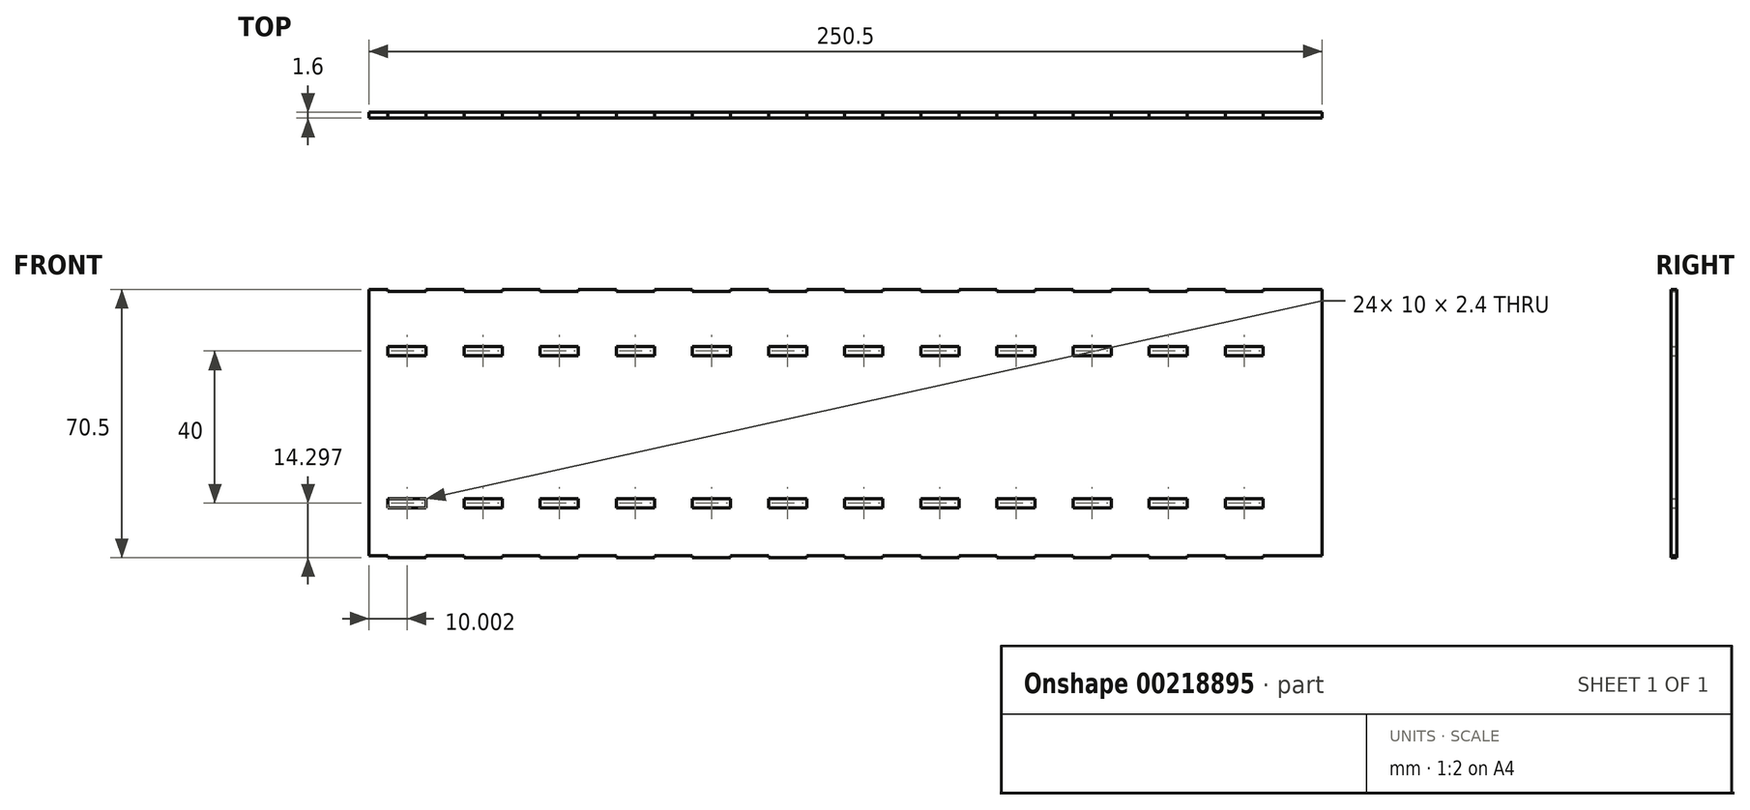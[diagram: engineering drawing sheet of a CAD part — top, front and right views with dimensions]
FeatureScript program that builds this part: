
annotation { "Feature Type Name" : "Feature", "Feature Type Description" : "" }
export const myFeature = defineFeature(function(context is Context, id is Id, definition is map)
    precondition{}
    {
        {
            var Q0;
            Q0=qCreatedBy(makeId("Front.planeOp"),FACE);
            var sketch = newSketch(context, id + "F0", { "sketchPlane" : qUnion([Q0])});
            skLineSegment(sketch, "E0.top", {"start": v(-125.84, -55.1) * mm, "end": v(-120.84, -55.1) * mm});
            skLineSegment(sketch, "E0.left", {"start": v(-125.84, 14.9) * mm, "end": v(-125.84, -55.1) * mm});
            skLineSegment(sketch, "E0.right", {"start": v(124.66, 14.9) * mm, "end": v(124.66, -55.1) * mm});
            skLineSegment(sketch, "E1.bottom", {"start": v(-120.84, -0.1) * mm, "end": v(-110.84, -0.1) * mm});
            skLineSegment(sketch, "E1.top", {"start": v(-120.84, -2.5) * mm, "end": v(-110.84, -2.5) * mm});
            skLineSegment(sketch, "E1.left", {"start": v(-120.84, -0.1) * mm, "end": v(-120.84, -2.5) * mm});
            skLineSegment(sketch, "E1.right", {"start": v(-110.84, -0.1) * mm, "end": v(-110.84, -2.5) * mm});
            skLineSegment(sketch, "E2.bottom", {"start": v(-120.84, -40.1) * mm, "end": v(-110.84, -40.1) * mm});
            skLineSegment(sketch, "E2.top", {"start": v(-120.84, -42.5) * mm, "end": v(-110.84, -42.5) * mm});
            skLineSegment(sketch, "E2.left", {"start": v(-120.84, -40.1) * mm, "end": v(-120.84, -42.5) * mm});
            skLineSegment(sketch, "E2.right", {"start": v(-110.84, -40.1) * mm, "end": v(-110.84, -42.5) * mm});
            skLineSegment(sketch, "E3.1.0.0", {"start": v(-100.84, -0.1) * mm, "end": v(-90.84, -0.1) * mm});
            skLineSegment(sketch, "E3.1.0.1", {"start": v(-100.84, -2.5) * mm, "end": v(-90.84, -2.5) * mm});
            skLineSegment(sketch, "E3.1.0.2", {"start": v(-90.84, -0.1) * mm, "end": v(-90.84, -2.5) * mm});
            skLineSegment(sketch, "E3.1.0.3", {"start": v(-100.84, -0.1) * mm, "end": v(-100.84, -2.5) * mm});
            skLineSegment(sketch, "E3.1.0.4", {"start": v(-100.84, -42.5) * mm, "end": v(-90.84, -42.5) * mm});
            skLineSegment(sketch, "E3.1.0.5", {"start": v(-100.84, -40.1) * mm, "end": v(-90.84, -40.1) * mm});
            skLineSegment(sketch, "E3.1.0.6", {"start": v(-90.84, -40.1) * mm, "end": v(-90.84, -42.5) * mm});
            skLineSegment(sketch, "E3.1.0.7", {"start": v(-100.84, -40.1) * mm, "end": v(-100.84, -42.5) * mm});
            skLineSegment(sketch, "E3.2.0.0", {"start": v(-80.84, -0.1) * mm, "end": v(-70.84, -0.1) * mm});
            skLineSegment(sketch, "E3.2.0.1", {"start": v(-80.84, -2.5) * mm, "end": v(-70.84, -2.5) * mm});
            skLineSegment(sketch, "E3.2.0.2", {"start": v(-70.84, -0.1) * mm, "end": v(-70.84, -2.5) * mm});
            skLineSegment(sketch, "E3.2.0.3", {"start": v(-80.84, -0.1) * mm, "end": v(-80.84, -2.5) * mm});
            skLineSegment(sketch, "E3.2.0.4", {"start": v(-80.84, -42.5) * mm, "end": v(-70.84, -42.5) * mm});
            skLineSegment(sketch, "E3.2.0.5", {"start": v(-80.84, -40.1) * mm, "end": v(-70.84, -40.1) * mm});
            skLineSegment(sketch, "E3.2.0.6", {"start": v(-70.84, -40.1) * mm, "end": v(-70.84, -42.5) * mm});
            skLineSegment(sketch, "E3.2.0.7", {"start": v(-80.84, -40.1) * mm, "end": v(-80.84, -42.5) * mm});
            skLineSegment(sketch, "E3.3.0.0", {"start": v(-60.84, -0.1) * mm, "end": v(-50.84, -0.1) * mm});
            skLineSegment(sketch, "E3.3.0.1", {"start": v(-60.84, -2.5) * mm, "end": v(-50.84, -2.5) * mm});
            skLineSegment(sketch, "E3.3.0.2", {"start": v(-50.84, -0.1) * mm, "end": v(-50.84, -2.5) * mm});
            skLineSegment(sketch, "E3.3.0.3", {"start": v(-60.84, -0.1) * mm, "end": v(-60.84, -2.5) * mm});
            skLineSegment(sketch, "E3.3.0.4", {"start": v(-60.84, -42.5) * mm, "end": v(-50.84, -42.5) * mm});
            skLineSegment(sketch, "E3.3.0.5", {"start": v(-60.84, -40.1) * mm, "end": v(-50.84, -40.1) * mm});
            skLineSegment(sketch, "E3.3.0.6", {"start": v(-50.84, -40.1) * mm, "end": v(-50.84, -42.5) * mm});
            skLineSegment(sketch, "E3.3.0.7", {"start": v(-60.84, -40.1) * mm, "end": v(-60.84, -42.5) * mm});
            skLineSegment(sketch, "E3.4.0.0", {"start": v(-40.84, -0.1) * mm, "end": v(-30.84, -0.1) * mm});
            skLineSegment(sketch, "E3.4.0.1", {"start": v(-40.84, -2.5) * mm, "end": v(-30.84, -2.5) * mm});
            skLineSegment(sketch, "E3.4.0.2", {"start": v(-30.84, -0.1) * mm, "end": v(-30.84, -2.5) * mm});
            skLineSegment(sketch, "E3.4.0.3", {"start": v(-40.84, -0.1) * mm, "end": v(-40.84, -2.5) * mm});
            skLineSegment(sketch, "E3.4.0.4", {"start": v(-40.84, -42.5) * mm, "end": v(-30.84, -42.5) * mm});
            skLineSegment(sketch, "E3.4.0.5", {"start": v(-40.84, -40.1) * mm, "end": v(-30.84, -40.1) * mm});
            skLineSegment(sketch, "E3.4.0.6", {"start": v(-30.84, -40.1) * mm, "end": v(-30.84, -42.5) * mm});
            skLineSegment(sketch, "E3.4.0.7", {"start": v(-40.84, -40.1) * mm, "end": v(-40.84, -42.5) * mm});
            skLineSegment(sketch, "E3.5.0.0", {"start": v(-20.84, -0.1) * mm, "end": v(-10.84, -0.1) * mm});
            skLineSegment(sketch, "E3.5.0.1", {"start": v(-20.84, -2.5) * mm, "end": v(-10.84, -2.5) * mm});
            skLineSegment(sketch, "E3.5.0.2", {"start": v(-10.84, -0.1) * mm, "end": v(-10.84, -2.5) * mm});
            skLineSegment(sketch, "E3.5.0.3", {"start": v(-20.84, -0.1) * mm, "end": v(-20.84, -2.5) * mm});
            skLineSegment(sketch, "E3.5.0.4", {"start": v(-20.84, -42.5) * mm, "end": v(-10.84, -42.5) * mm});
            skLineSegment(sketch, "E3.5.0.5", {"start": v(-20.84, -40.1) * mm, "end": v(-10.84, -40.1) * mm});
            skLineSegment(sketch, "E3.5.0.6", {"start": v(-10.84, -40.1) * mm, "end": v(-10.84, -42.5) * mm});
            skLineSegment(sketch, "E3.5.0.7", {"start": v(-20.84, -40.1) * mm, "end": v(-20.84, -42.5) * mm});
            skLineSegment(sketch, "E3.6.0.0", {"start": v(-0.84, -0.1) * mm, "end": v(9.16, -0.1) * mm});
            skLineSegment(sketch, "E3.6.0.1", {"start": v(-0.84, -2.5) * mm, "end": v(9.16, -2.5) * mm});
            skLineSegment(sketch, "E3.6.0.2", {"start": v(9.16, -0.1) * mm, "end": v(9.16, -2.5) * mm});
            skLineSegment(sketch, "E3.6.0.3", {"start": v(-0.84, -0.1) * mm, "end": v(-0.84, -2.5) * mm});
            skLineSegment(sketch, "E3.6.0.4", {"start": v(-0.84, -42.5) * mm, "end": v(9.16, -42.5) * mm});
            skLineSegment(sketch, "E3.6.0.5", {"start": v(-0.84, -40.1) * mm, "end": v(9.16, -40.1) * mm});
            skLineSegment(sketch, "E3.6.0.6", {"start": v(9.16, -40.1) * mm, "end": v(9.16, -42.5) * mm});
            skLineSegment(sketch, "E3.6.0.7", {"start": v(-0.84, -40.1) * mm, "end": v(-0.84, -42.5) * mm});
            skLineSegment(sketch, "E3.7.0.0", {"start": v(19.16, -0.1) * mm, "end": v(29.16, -0.1) * mm});
            skLineSegment(sketch, "E3.7.0.1", {"start": v(19.16, -2.5) * mm, "end": v(29.16, -2.5) * mm});
            skLineSegment(sketch, "E3.7.0.2", {"start": v(29.16, -0.1) * mm, "end": v(29.16, -2.5) * mm});
            skLineSegment(sketch, "E3.7.0.3", {"start": v(19.16, -0.1) * mm, "end": v(19.16, -2.5) * mm});
            skLineSegment(sketch, "E3.7.0.4", {"start": v(19.16, -42.5) * mm, "end": v(29.16, -42.5) * mm});
            skLineSegment(sketch, "E3.7.0.5", {"start": v(19.16, -40.1) * mm, "end": v(29.16, -40.1) * mm});
            skLineSegment(sketch, "E3.7.0.6", {"start": v(29.16, -40.1) * mm, "end": v(29.16, -42.5) * mm});
            skLineSegment(sketch, "E3.7.0.7", {"start": v(19.16, -40.1) * mm, "end": v(19.16, -42.5) * mm});
            skLineSegment(sketch, "E3.8.0.0", {"start": v(39.16, -0.1) * mm, "end": v(49.16, -0.1) * mm});
            skLineSegment(sketch, "E3.8.0.1", {"start": v(39.16, -2.5) * mm, "end": v(49.16, -2.5) * mm});
            skLineSegment(sketch, "E3.8.0.2", {"start": v(49.16, -0.1) * mm, "end": v(49.16, -2.5) * mm});
            skLineSegment(sketch, "E3.8.0.3", {"start": v(39.16, -0.1) * mm, "end": v(39.16, -2.5) * mm});
            skLineSegment(sketch, "E3.8.0.4", {"start": v(39.16, -42.5) * mm, "end": v(49.16, -42.5) * mm});
            skLineSegment(sketch, "E3.8.0.5", {"start": v(39.16, -40.1) * mm, "end": v(49.16, -40.1) * mm});
            skLineSegment(sketch, "E3.8.0.6", {"start": v(49.16, -40.1) * mm, "end": v(49.16, -42.5) * mm});
            skLineSegment(sketch, "E3.8.0.7", {"start": v(39.16, -40.1) * mm, "end": v(39.16, -42.5) * mm});
            skLineSegment(sketch, "E3.9.0.0", {"start": v(59.16, -0.1) * mm, "end": v(69.16, -0.1) * mm});
            skLineSegment(sketch, "E3.9.0.1", {"start": v(59.16, -2.5) * mm, "end": v(69.16, -2.5) * mm});
            skLineSegment(sketch, "E3.9.0.2", {"start": v(69.16, -0.1) * mm, "end": v(69.16, -2.5) * mm});
            skLineSegment(sketch, "E3.9.0.3", {"start": v(59.16, -0.1) * mm, "end": v(59.16, -2.5) * mm});
            skLineSegment(sketch, "E3.9.0.4", {"start": v(59.16, -42.5) * mm, "end": v(69.16, -42.5) * mm});
            skLineSegment(sketch, "E3.9.0.5", {"start": v(59.16, -40.1) * mm, "end": v(69.16, -40.1) * mm});
            skLineSegment(sketch, "E3.9.0.6", {"start": v(69.16, -40.1) * mm, "end": v(69.16, -42.5) * mm});
            skLineSegment(sketch, "E3.9.0.7", {"start": v(59.16, -40.1) * mm, "end": v(59.16, -42.5) * mm});
            skLineSegment(sketch, "E3.10.0.0", {"start": v(79.16, -0.1) * mm, "end": v(89.16, -0.1) * mm});
            skLineSegment(sketch, "E3.10.0.1", {"start": v(79.16, -2.5) * mm, "end": v(89.16, -2.5) * mm});
            skLineSegment(sketch, "E3.10.0.2", {"start": v(89.16, -0.1) * mm, "end": v(89.16, -2.5) * mm});
            skLineSegment(sketch, "E3.10.0.3", {"start": v(79.16, -0.1) * mm, "end": v(79.16, -2.5) * mm});
            skLineSegment(sketch, "E3.10.0.4", {"start": v(79.16, -42.5) * mm, "end": v(89.16, -42.5) * mm});
            skLineSegment(sketch, "E3.10.0.5", {"start": v(79.16, -40.1) * mm, "end": v(89.16, -40.1) * mm});
            skLineSegment(sketch, "E3.10.0.6", {"start": v(89.16, -40.1) * mm, "end": v(89.16, -42.5) * mm});
            skLineSegment(sketch, "E3.10.0.7", {"start": v(79.16, -40.1) * mm, "end": v(79.16, -42.5) * mm});
            skLineSegment(sketch, "E3.11.0.0", {"start": v(99.16, -0.1) * mm, "end": v(109.16, -0.1) * mm});
            skLineSegment(sketch, "E3.11.0.1", {"start": v(99.16, -2.5) * mm, "end": v(109.16, -2.5) * mm});
            skLineSegment(sketch, "E3.11.0.2", {"start": v(109.16, -0.1) * mm, "end": v(109.16, -2.5) * mm});
            skLineSegment(sketch, "E3.11.0.3", {"start": v(99.16, -0.1) * mm, "end": v(99.16, -2.5) * mm});
            skLineSegment(sketch, "E3.11.0.4", {"start": v(99.16, -42.5) * mm, "end": v(109.16, -42.5) * mm});
            skLineSegment(sketch, "E3.11.0.5", {"start": v(99.16, -40.1) * mm, "end": v(109.16, -40.1) * mm});
            skLineSegment(sketch, "E3.11.0.6", {"start": v(109.16, -40.1) * mm, "end": v(109.16, -42.5) * mm});
            skLineSegment(sketch, "E3.11.0.7", {"start": v(99.16, -40.1) * mm, "end": v(99.16, -42.5) * mm});
            skLineSegment(sketch, "E3.direction1", {"start": v(-120.84, -0.1) * mm, "end": v(-100.84, -0.1) * mm, "construction": true});
            skLineSegment(sketch, "E4", {"start": v(-120.84, -55.1) * mm, "end": v(-120.84, -55.6) * mm});
            skLineSegment(sketch, "E5", {"start": v(-120.84, -55.6) * mm, "end": v(-110.84, -55.6) * mm});
            skLineSegment(sketch, "E6", {"start": v(-110.84, -55.6) * mm, "end": v(-110.84, -55.1) * mm});
            skLineSegment(sketch, "E7.trimOffspring", {"start": v(-110.84, -55.1) * mm, "end": v(-100.84, -55.1) * mm});
            skLineSegment(sketch, "E8.1.0.0", {"start": v(-100.84, -55.6) * mm, "end": v(-90.84, -55.6) * mm});
            skLineSegment(sketch, "E8.1.0.1", {"start": v(-90.84, -55.6) * mm, "end": v(-90.84, -55.1) * mm});
            skLineSegment(sketch, "E8.1.0.2", {"start": v(-100.84, -55.1) * mm, "end": v(-100.84, -55.6) * mm});
            skLineSegment(sketch, "E8.2.0.0", {"start": v(-80.84, -55.6) * mm, "end": v(-70.84, -55.6) * mm});
            skLineSegment(sketch, "E8.2.0.1", {"start": v(-70.84, -55.6) * mm, "end": v(-70.84, -55.1) * mm});
            skLineSegment(sketch, "E8.2.0.2", {"start": v(-80.84, -55.1) * mm, "end": v(-80.84, -55.6) * mm});
            skLineSegment(sketch, "E8.3.0.0", {"start": v(-60.84, -55.6) * mm, "end": v(-50.84, -55.6) * mm});
            skLineSegment(sketch, "E8.3.0.1", {"start": v(-50.84, -55.6) * mm, "end": v(-50.84, -55.1) * mm});
            skLineSegment(sketch, "E8.3.0.2", {"start": v(-60.84, -55.1) * mm, "end": v(-60.84, -55.6) * mm});
            skLineSegment(sketch, "E8.4.0.0", {"start": v(-40.84, -55.6) * mm, "end": v(-30.84, -55.6) * mm});
            skLineSegment(sketch, "E8.4.0.1", {"start": v(-30.84, -55.6) * mm, "end": v(-30.84, -55.1) * mm});
            skLineSegment(sketch, "E8.4.0.2", {"start": v(-40.84, -55.1) * mm, "end": v(-40.84, -55.6) * mm});
            skLineSegment(sketch, "E8.5.0.0", {"start": v(-20.84, -55.6) * mm, "end": v(-10.84, -55.6) * mm});
            skLineSegment(sketch, "E8.5.0.1", {"start": v(-10.84, -55.6) * mm, "end": v(-10.84, -55.1) * mm});
            skLineSegment(sketch, "E8.5.0.2", {"start": v(-20.84, -55.1) * mm, "end": v(-20.84, -55.6) * mm});
            skLineSegment(sketch, "E8.6.0.0", {"start": v(-0.84, -55.6) * mm, "end": v(9.16, -55.6) * mm});
            skLineSegment(sketch, "E8.6.0.1", {"start": v(9.16, -55.6) * mm, "end": v(9.16, -55.1) * mm});
            skLineSegment(sketch, "E8.6.0.2", {"start": v(-0.84, -55.1) * mm, "end": v(-0.84, -55.6) * mm});
            skLineSegment(sketch, "E8.7.0.0", {"start": v(19.16, -55.6) * mm, "end": v(29.16, -55.6) * mm});
            skLineSegment(sketch, "E8.7.0.1", {"start": v(29.16, -55.6) * mm, "end": v(29.16, -55.1) * mm});
            skLineSegment(sketch, "E8.7.0.2", {"start": v(19.16, -55.1) * mm, "end": v(19.16, -55.6) * mm});
            skLineSegment(sketch, "E8.8.0.0", {"start": v(39.16, -55.6) * mm, "end": v(49.16, -55.6) * mm});
            skLineSegment(sketch, "E8.8.0.1", {"start": v(49.16, -55.6) * mm, "end": v(49.16, -55.1) * mm});
            skLineSegment(sketch, "E8.8.0.2", {"start": v(39.16, -55.1) * mm, "end": v(39.16, -55.6) * mm});
            skLineSegment(sketch, "E8.9.0.0", {"start": v(59.16, -55.6) * mm, "end": v(69.16, -55.6) * mm});
            skLineSegment(sketch, "E8.9.0.1", {"start": v(69.16, -55.6) * mm, "end": v(69.16, -55.1) * mm});
            skLineSegment(sketch, "E8.9.0.2", {"start": v(59.16, -55.1) * mm, "end": v(59.16, -55.6) * mm});
            skLineSegment(sketch, "E8.10.0.0", {"start": v(79.16, -55.6) * mm, "end": v(89.16, -55.6) * mm});
            skLineSegment(sketch, "E8.10.0.1", {"start": v(89.16, -55.6) * mm, "end": v(89.16, -55.1) * mm});
            skLineSegment(sketch, "E8.10.0.2", {"start": v(79.16, -55.1) * mm, "end": v(79.16, -55.6) * mm});
            skLineSegment(sketch, "E8.11.0.0", {"start": v(99.16, -55.6) * mm, "end": v(109.16, -55.6) * mm});
            skLineSegment(sketch, "E8.11.0.1", {"start": v(109.16, -55.6) * mm, "end": v(109.16, -55.1) * mm});
            skLineSegment(sketch, "E8.11.0.2", {"start": v(99.16, -55.1) * mm, "end": v(99.16, -55.6) * mm});
            skLineSegment(sketch, "E8.direction1", {"start": v(-120.84, -55.6) * mm, "end": v(-100.84, -55.6) * mm, "construction": true});
            skLineSegment(sketch, "E9.trimOffspring", {"start": v(-90.84, -55.1) * mm, "end": v(-80.84, -55.1) * mm});
            skLineSegment(sketch, "E10.trimOffspring", {"start": v(-70.84, -55.1) * mm, "end": v(-60.84, -55.1) * mm});
            skLineSegment(sketch, "E11.trimOffspring", {"start": v(-50.84, -55.1) * mm, "end": v(-40.84, -55.1) * mm});
            skLineSegment(sketch, "E12.trimOffspring", {"start": v(-30.84, -55.1) * mm, "end": v(-20.84, -55.1) * mm});
            skLineSegment(sketch, "E13.trimOffspring", {"start": v(-10.84, -55.1) * mm, "end": v(-0.84, -55.1) * mm});
            skLineSegment(sketch, "E14.trimOffspring", {"start": v(9.16, -55.1) * mm, "end": v(19.16, -55.1) * mm});
            skLineSegment(sketch, "E15.trimOffspring", {"start": v(29.16, -55.1) * mm, "end": v(39.16, -55.1) * mm});
            skLineSegment(sketch, "E16.trimOffspring", {"start": v(49.16, -55.1) * mm, "end": v(59.16, -55.1) * mm});
            skLineSegment(sketch, "E17.trimOffspring", {"start": v(69.16, -55.1) * mm, "end": v(79.16, -55.1) * mm});
            skLineSegment(sketch, "E18.trimOffspring", {"start": v(89.16, -55.1) * mm, "end": v(99.16, -55.1) * mm});
            skLineSegment(sketch, "E19.trimOffspring", {"start": v(109.16, -55.1) * mm, "end": v(124.66, -55.1) * mm});
            skLineSegment(sketch, "E20", {"start": v(-120.84, 14.9) * mm, "end": v(-120.84, 14.4) * mm});
            skLineSegment(sketch, "E21", {"start": v(-120.84, 14.4) * mm, "end": v(-110.84, 14.4) * mm});
            skLineSegment(sketch, "E22", {"start": v(-110.84, 14.4) * mm, "end": v(-110.84, 14.9) * mm});
            skLineSegment(sketch, "E23", {"start": v(-110.84, 14.9) * mm, "end": v(-100.84, 14.9) * mm});
            skLineSegment(sketch, "E24.1.0.0", {"start": v(-100.84, 14.9) * mm, "end": v(-100.84, 14.4) * mm});
            skLineSegment(sketch, "E24.1.0.1", {"start": v(-100.84, 14.4) * mm, "end": v(-90.84, 14.4) * mm});
            skLineSegment(sketch, "E24.1.0.2", {"start": v(-90.84, 14.4) * mm, "end": v(-90.84, 14.9) * mm});
            skLineSegment(sketch, "E24.1.0.3", {"start": v(-90.84, 14.9) * mm, "end": v(-80.84, 14.9) * mm});
            skLineSegment(sketch, "E24.2.0.0", {"start": v(-80.84, 14.9) * mm, "end": v(-80.84, 14.4) * mm});
            skLineSegment(sketch, "E24.2.0.1", {"start": v(-80.84, 14.4) * mm, "end": v(-70.84, 14.4) * mm});
            skLineSegment(sketch, "E24.2.0.2", {"start": v(-70.84, 14.4) * mm, "end": v(-70.84, 14.9) * mm});
            skLineSegment(sketch, "E24.2.0.3", {"start": v(-70.84, 14.9) * mm, "end": v(-60.84, 14.9) * mm});
            skLineSegment(sketch, "E24.3.0.0", {"start": v(-60.84, 14.9) * mm, "end": v(-60.84, 14.4) * mm});
            skLineSegment(sketch, "E24.3.0.1", {"start": v(-60.84, 14.4) * mm, "end": v(-50.84, 14.4) * mm});
            skLineSegment(sketch, "E24.3.0.2", {"start": v(-50.84, 14.4) * mm, "end": v(-50.84, 14.9) * mm});
            skLineSegment(sketch, "E24.3.0.3", {"start": v(-50.84, 14.9) * mm, "end": v(-40.84, 14.9) * mm});
            skLineSegment(sketch, "E24.4.0.0", {"start": v(-40.84, 14.9) * mm, "end": v(-40.84, 14.4) * mm});
            skLineSegment(sketch, "E24.4.0.1", {"start": v(-40.84, 14.4) * mm, "end": v(-30.84, 14.4) * mm});
            skLineSegment(sketch, "E24.4.0.2", {"start": v(-30.84, 14.4) * mm, "end": v(-30.84, 14.9) * mm});
            skLineSegment(sketch, "E24.4.0.3", {"start": v(-30.84, 14.9) * mm, "end": v(-20.84, 14.9) * mm});
            skLineSegment(sketch, "E24.5.0.0", {"start": v(-20.84, 14.9) * mm, "end": v(-20.84, 14.4) * mm});
            skLineSegment(sketch, "E24.5.0.1", {"start": v(-20.84, 14.4) * mm, "end": v(-10.84, 14.4) * mm});
            skLineSegment(sketch, "E24.5.0.2", {"start": v(-10.84, 14.4) * mm, "end": v(-10.84, 14.9) * mm});
            skLineSegment(sketch, "E24.5.0.3", {"start": v(-10.84, 14.9) * mm, "end": v(-0.84, 14.9) * mm});
            skLineSegment(sketch, "E24.6.0.0", {"start": v(-0.84, 14.9) * mm, "end": v(-0.84, 14.4) * mm});
            skLineSegment(sketch, "E24.6.0.1", {"start": v(-0.84, 14.4) * mm, "end": v(9.16, 14.4) * mm});
            skLineSegment(sketch, "E24.6.0.2", {"start": v(9.16, 14.4) * mm, "end": v(9.16, 14.9) * mm});
            skLineSegment(sketch, "E24.6.0.3", {"start": v(9.16, 14.9) * mm, "end": v(19.16, 14.9) * mm});
            skLineSegment(sketch, "E24.7.0.0", {"start": v(19.16, 14.9) * mm, "end": v(19.16, 14.4) * mm});
            skLineSegment(sketch, "E24.7.0.1", {"start": v(19.16, 14.4) * mm, "end": v(29.16, 14.4) * mm});
            skLineSegment(sketch, "E24.7.0.2", {"start": v(29.16, 14.4) * mm, "end": v(29.16, 14.9) * mm});
            skLineSegment(sketch, "E24.7.0.3", {"start": v(29.16, 14.9) * mm, "end": v(39.16, 14.9) * mm});
            skLineSegment(sketch, "E24.8.0.0", {"start": v(39.16, 14.9) * mm, "end": v(39.16, 14.4) * mm});
            skLineSegment(sketch, "E24.8.0.1", {"start": v(39.16, 14.4) * mm, "end": v(49.16, 14.4) * mm});
            skLineSegment(sketch, "E24.8.0.2", {"start": v(49.16, 14.4) * mm, "end": v(49.16, 14.9) * mm});
            skLineSegment(sketch, "E24.8.0.3", {"start": v(49.16, 14.9) * mm, "end": v(59.16, 14.9) * mm});
            skLineSegment(sketch, "E24.9.0.0", {"start": v(59.16, 14.9) * mm, "end": v(59.16, 14.4) * mm});
            skLineSegment(sketch, "E24.9.0.1", {"start": v(59.16, 14.4) * mm, "end": v(69.16, 14.4) * mm});
            skLineSegment(sketch, "E24.9.0.2", {"start": v(69.16, 14.4) * mm, "end": v(69.16, 14.9) * mm});
            skLineSegment(sketch, "E24.9.0.3", {"start": v(69.16, 14.9) * mm, "end": v(79.16, 14.9) * mm});
            skLineSegment(sketch, "E24.10.0.0", {"start": v(79.16, 14.9) * mm, "end": v(79.16, 14.4) * mm});
            skLineSegment(sketch, "E24.10.0.1", {"start": v(79.16, 14.4) * mm, "end": v(89.16, 14.4) * mm});
            skLineSegment(sketch, "E24.10.0.2", {"start": v(89.16, 14.4) * mm, "end": v(89.16, 14.9) * mm});
            skLineSegment(sketch, "E24.10.0.3", {"start": v(89.16, 14.9) * mm, "end": v(99.16, 14.9) * mm});
            skLineSegment(sketch, "E24.11.0.0", {"start": v(99.16, 14.9) * mm, "end": v(99.16, 14.4) * mm});
            skLineSegment(sketch, "E24.11.0.1", {"start": v(99.16, 14.4) * mm, "end": v(109.16, 14.4) * mm});
            skLineSegment(sketch, "E24.11.0.2", {"start": v(109.16, 14.4) * mm, "end": v(109.16, 14.9) * mm});
            skLineSegment(sketch, "E24.11.0.3", {"start": v(109.16, 14.9) * mm, "end": v(119.16, 14.9) * mm});
            skLineSegment(sketch, "E24.direction1", {"start": v(-120.84, 14.4) * mm, "end": v(-100.84, 14.4) * mm, "construction": true});
            skLineSegment(sketch, "E25", {"start": v(-125.84, 14.9) * mm, "end": v(-120.84, 14.9) * mm});
            skLineSegment(sketch, "E26", {"start": v(119.16, 14.9) * mm, "end": v(124.66, 14.9) * mm});
            skLineSegment(sketch, "E27", {"start": v(-120.84, -1.3) * mm, "end": v(-110.84, -1.3) * mm, "construction": true});
            skPoint(sketch, "E28", {"position": v(-115.84, -1.3) * mm});
            skSolve(sketch);
        }
        {
            var Q0;
            Q0=makeQuery(id+"F0.imprint","IMPRINT",FACE,{"disambiguationData":[TD([[makeQuery(id+"F0.imprint","IMPRINT",EDGE,{"derivedFrom":sQuery(id+"F0.wireOp",EDGE,"E0.top")}),1.0]])]});
            extrude(context, id + "F1", {"entities" : qUnion([Q0]), "depth" : 1.6 * mm});
        }
    });
